# Revit family: QF_GIORIK_KHG101_KTG101_KHG101W_KTG101W
name_source: partatom
category: Specialty Equipment
revit_build: Autodesk Revit 2014 (Build: 20140709_2115(x64)
units: mm (PartAtom-declared; Revit-internal decimal feet)

## types (4) — shared parameters
Assembly Code = E1090320
Cold Water Connection Height = 98 mm  [stored 0.321522 ft]
Cold Water Size = 1"
Cold Water Temperature Recommended = 0 °C
Cycle = 50 Hz
FL Amps = 0 A
Gas Connection Height = 954 mm  [stored 3.12992 ft]
Gas Input = 11000 W
Gas KW = 11
Gas Size = 1"
HP = 0
Indirect Waste Connection Height = 89 mm  [stored 0.291995 ft]
Indirect Waste Flow = 0.0 L/s
Indirect Waste Size = 1 1/2"
Manufacturer = GIORIK
Max Overcurrent Protection = 16 A
Min Ckt Ampacity = 0 A
Phase = 1
Touch screen control = Yes
URL = www.giorik.com
Volts = 230 V
Waste Water Discharge Temperature = 0 °C
Weight in Pounds = 260.145

## per-type parameters (varying)
| type | Apparent Power | Description | Watts |
| KHG101 | 1600 VA | GAS OVEN 10 GN 1/1 COMBINED CONVECTION/STEAM TOUCH SCREEN CONTROL - HIGH EFFICIENCY BOILER VERSION | 1600 W |
| KTG101 | 600 VA | GAS OVEN 10 GN 1/1 COMBINED CONVECTION/STEAM TOUCH SCREEN CONTROL - DIRECT STEAM VERSION | 600 W |
| KHG101W | 1600 VA | GAS OVEN 10 GN 1/1 COMBINED CONVECTION/STEAM TOUCH SCREEN CONTROL - HIGH EFFICIENCY BOILER VERSION | 1600 W |
| KTG101W | 600 VA | GAS OVEN 10 GN 1/1 COMBINED CONVECTION/STEAM TOUCH SCREEN CONTROL - DIRECT STEAM VERSION | 600 W |

note: column(s) folded — value = type name in every type: Model

note: [stored X ft] marks values corroborated as IEEE doubles in the binary element streams (Revit-internal decimal feet)

## geometry (parser evidence)
native form markers: Blend x6, Sweep x1
no freeform markers — native parametric forms only
